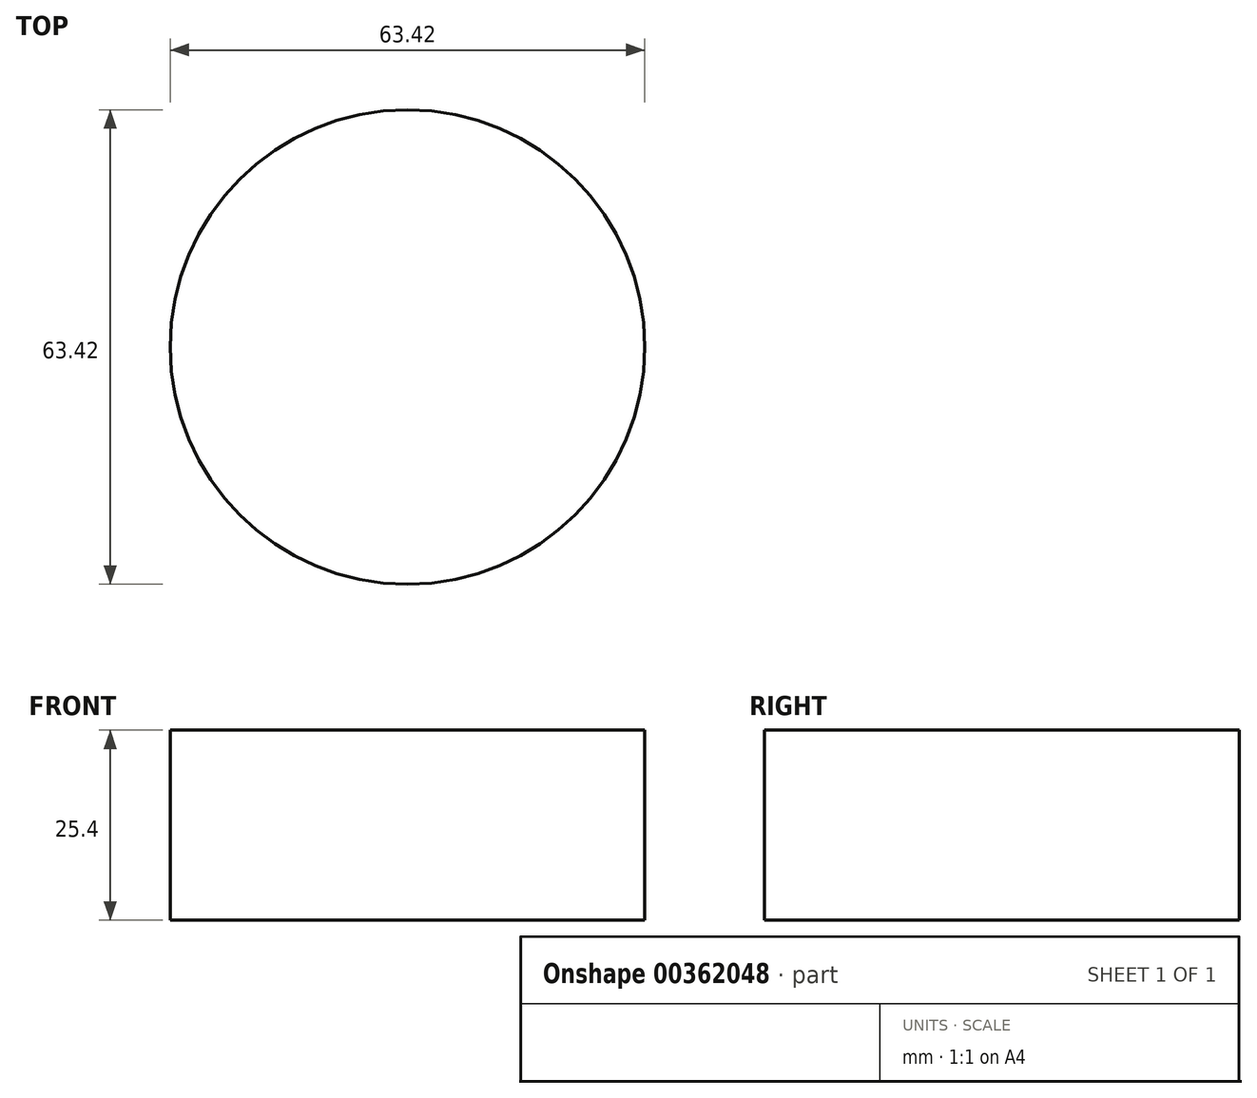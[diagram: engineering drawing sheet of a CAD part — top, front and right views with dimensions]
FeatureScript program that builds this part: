
annotation { "Feature Type Name" : "Feature", "Feature Type Description" : "" }
export const myFeature = defineFeature(function(context is Context, id is Id, definition is map)
    precondition{}
    {
        {
            var Q0;
            Q0=qCreatedBy(makeId("Top.planeOp"),FACE);
            var sketch = newSketch(context, id + "F0", { "sketchPlane" : qUnion([Q0])});
            skCircle(sketch, "E0", {"center": v(0, 0) * mm, "radius": 31.7 * mm});
            skSolve(sketch);
        }
        {
            var Q0;
            Q0 = qSketchRegion(id + "F0", true);
            extrude(context, id + "F1", {"entities" : qUnion([Q0]), "depth" : 25.4 * mm});
        }
    });
